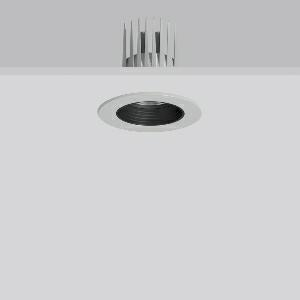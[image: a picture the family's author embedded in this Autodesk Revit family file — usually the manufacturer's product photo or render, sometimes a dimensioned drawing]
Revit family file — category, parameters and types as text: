
# Revit family: heledon_mini_e_901747_004_2_7db3
name_source: partatom
category: Lighting Fixtures
units: mm (PartAtom-declared; Revit-internal decimal feet)

## family parameters
Cut with Voids When Loaded = No
Host = Face
Light Source = No
Part Type = Normal
Room Calculation Point = No
Round Connector Dimension = Use Diameter
Shared = No

## types (1)
- HELEDON mini E (1 x LED Modul 927, 1850 lm, 2700)
    Apparent Load = 20 VA
    Approval mark = CE
    CIE Flux Codes = 95 100 100 100 100
    Color Rendering = 92
    Color Temperature = 2700
    Default Elevation = 1800 mm
    Description = Series: HELEDON mini
Round recessed downlight. Housing: die-cast aluminium, powder-coated. Black plastic ring and recessed LED to prevent glare from the side. Optical assembly with lens made of plastic (polycarbonate) for the best homogeneous light distribution - can be changed without tools. Best colour rendering index Ra>90. Suitable for Recessed ceiling mounting. Installation without tools thanks to spring fastening system. Including separate LED converter with connecting cable 600 mm.High quality converter without flickering and stroboscopic effect. Through-wiring box (5 pole) available as accessory. The following accessories can be mounted without use of tools: interchangeable lenses, decorative glasses, honeycomb louvre, clear and frosted diffusers, white interchangeable plastic ring. 
Colour: silver
Diameter: 124 mm
Height: 3 mm
Cut-out diameter: 114 mm
Recess height: 170 mm
Luminaire: recess height: 120 mm
Lamp: LED
Socket: without socket
Colour temperature: 2700K
Colour rendering index (CRI): 92
System power: 20 W
Rated luminous flux: 1850 lm
Luminous efficiency: 93 lm/W
Control gear: Regulated power supply
Protection class: II
Type of protection: IP 20
    Height = 0 mm  [stored 0 ft]
    Lamp = 1 x LED Modul 927
    Lamp Light Flux = 1850 lm
    Lamp count = 1
    Length = 124 mm  [stored 0.406824 ft]
    Lifetime = 50000 h
    Luminous efficacy = 93 lm/W
    Manufacturer = RZB
    ModVariant = No
    Model = 901747.004.2
    Mounting Place = Ceiling
    Mounting Type = Recessed
    Number of Poles = 1
    OnlyDefault = Yes
    Power Factor = 1
    Product Name = HELEDON mini E
    Product group = Recessed downlights
    ProductGroupID = 402
    Protection Class = Protection class II
    Protection Degree = IP 20
    RLX_Detail_Level = 1
    RLX_Emergency_Light_Flux = 0 lm
    RLX_Emergency_Type = 0
    RLX_Emergency_Type_DB = No
    RlxData = <blob elided: 135413 chars, md5=eb22da83>
    Socket = socket
    Standby Power = 0 W
    System Light Flux = 1850 lm
    System Power = 20 W
    Type Comments = Product without accessories
    Type Image = 901656.004.jpg
    URL = http://relux.com
    VarID = ---
    Voltage = 230 V
    Voltage Range = 220-240 V
    Weight = 0.00 kg
    Width = 0 mm  [stored 0 ft]

note: [stored X ft] marks values corroborated as IEEE doubles in the binary element streams (Revit-internal decimal feet)

## geometry (parser evidence)
native form markers: Blend x4, Sweep x10
no freeform markers — native parametric forms only
